# Revit family: BFS-BEL-DSD-ME-Gong
name_source: partatom
category: Fire Alarm Devices
revit_build: Autodesk Revit 2018 (Build: 20170223_1515(x64)
units: mm (PartAtom-declared; Revit-internal decimal feet)

## family parameters
Cut with Voids When Loaded = No
Host = Face
Maintain Annotation Orientation = No
OmniClass Number = 23.29.31.15.11
OmniClass Title = Audible Fire Notification Devices Bell
Part Type = Normal
Room Calculation Point = No
Round Connector Dimension = Use Diameter
Shared = No

## types (3) — shared parameters
Red_255000000 = ME_Red_255-000-000
Silver_200200200 = ME_Silver_200-200-200
White_255255255 = ME_White_255-255-255
zero-valued in all types: DSD.BFS.Height, DSD.BFS.Length, DSD.BFS.Width

## per-type parameters (varying)
| type | Default Elevation | Depth | Diameter | r/2 |
| 150mm | 1219 mm | 64 mm  [stored 0.209974 ft] | 150 mm | 75 mm |
| 250mm | 0 mm  [stored 0 ft] | 81 mm | 250 mm  [stored 0.82021 ft] | 125 mm  [stored 0.410105 ft] |
| 200mm | 1219 mm | 73 mm | 200 mm  [stored 0.656168 ft] | 100 mm  [stored 0.328084 ft] |

note: [stored X ft] marks values corroborated as IEEE doubles in the binary element streams (Revit-internal decimal feet)

## geometry (parser evidence)
native form markers: Sweep x6
no freeform markers — native parametric forms only
